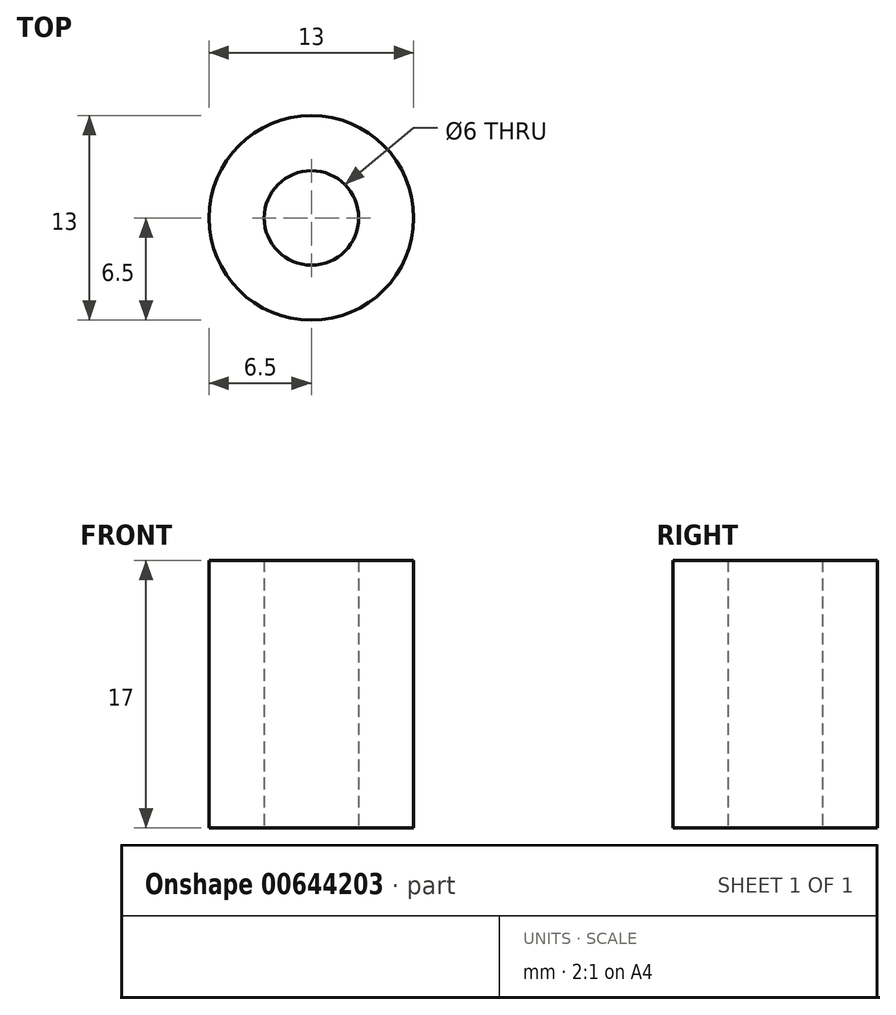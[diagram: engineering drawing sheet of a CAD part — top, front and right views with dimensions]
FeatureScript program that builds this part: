
annotation { "Feature Type Name" : "Feature", "Feature Type Description" : "" }
export const myFeature = defineFeature(function(context is Context, id is Id, definition is map)
    precondition{}
    {
        {
            assignVariable(context, id + "F0", {"name" : "Thickness", "anyValue" : 17});
        }
        {
            var Q0;
            Q0=qCreatedBy(makeId("Top.planeOp"),FACE);
            var sketch = newSketch(context, id + "F1", { "sketchPlane" : qUnion([Q0])});
            skCircle(sketch, "E0", {"center": v(0, 0) * mm, "radius": 3 * mm});
            skCircle(sketch, "E1", {"center": v(0, 0) * mm, "radius": 6.5 * mm});
            skSolve(sketch);
        }
        {
            var Q0;
            Q0=makeQuery(id+"F1.imprint","IMPRINT",FACE,{"disambiguationData":[TD([[makeQuery(id+"F1.imprint","IMPRINT",EDGE,{"derivedFrom":sQuery(id+"F1.wireOp",EDGE,"E0")}),-1.0]])]});
            extrude(context, id + "F2", {"entities" : qUnion([Q0]), "depth" : (getVariable(context, 'Thickness')) * mm, "offsetDistance" : 25 * mm});
        }
    });
